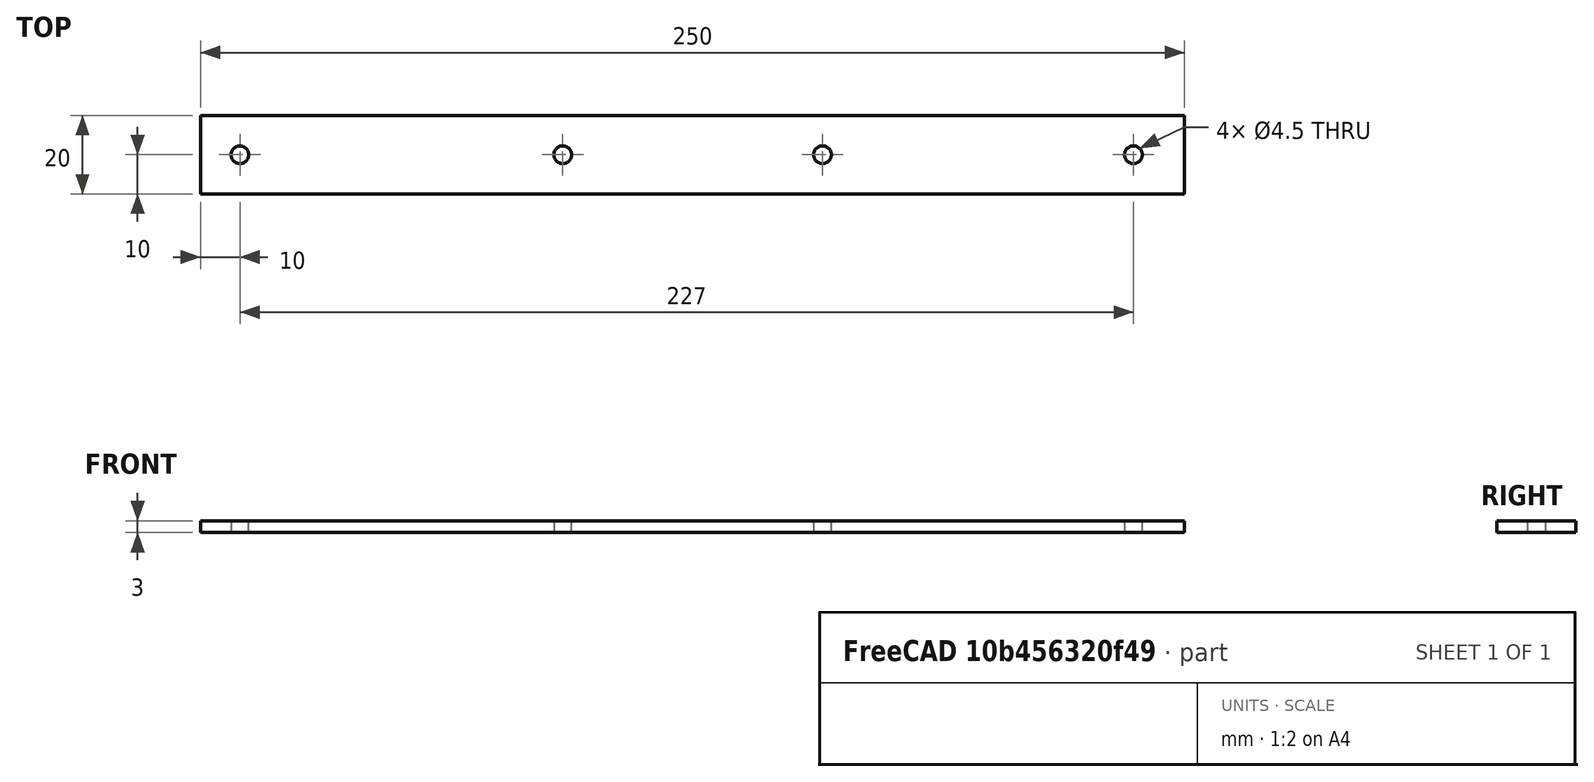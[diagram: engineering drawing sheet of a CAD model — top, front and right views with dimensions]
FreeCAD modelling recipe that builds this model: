
FCSTD DOCUMENT  (FreeCAD 0.21R33668 +26 (Git))
Label: 1-folding-hinge-rear-bar
License: All rights reserved
LicenseURL: http://en.wikipedia.org/wiki/All_rights_reserved
objects: PartDesign::SubtractiveCylinder×4, PartDesign::AdditiveBox×1, PartDesign::Body×1
note: 11 computed .brp shape members not serialized (recipe doc carries the construction recipe); baked Part::Feature solids carry a one-line shape summary decoded from their .brp

FEATURE [PartDesign::AdditiveBox] Box  label="bar"
  AttacherType = Attacher::AttachEngine3D
  Height = 3
  Length = 250
  Width = 20
FEATURE [PartDesign::SubtractiveCylinder] Cylinder  label="mp1"
  Angle = 360
  AttacherType = Attacher::AttachEngine3D
  AttachmentOffset = pos=(10,10,-3) rot=(0,0,1;0rad)
  BaseFeature = -> Box
  FirstAngle = 0
  Height = 3
  MapMode = 5
  Placement = pos=(10,10,0) rot=(0,0,1;0rad)
  Radius = 2.25
  SecondAngle = 0
  Support = -> [Box]
FEATURE [PartDesign::SubtractiveCylinder] Cylinder001  label="mp2"
  Angle = 360
  AttacherType = Attacher::AttachEngine3D
  AttachmentOffset = pos=(227,0,-3) rot=(0,0,1;0rad)
  BaseFeature = -> Cylinder
  FirstAngle = 0
  Height = 3
  MapMode = 5
  Placement = pos=(237,10,0) rot=(0,0,1;0rad)
  Radius = 2.25
  SecondAngle = 0
  Support = -> [Cylinder]
FEATURE [PartDesign::SubtractiveCylinder] Cylinder002  label="hinge-mp1"
  Angle = 360
  AttacherType = Attacher::AttachEngine3D
  AttachmentOffset = pos=(-145,0,-3) rot=(0,0,1;0rad)
  BaseFeature = -> Cylinder001
  FirstAngle = 0
  Height = 3
  MapMode = 5
  Placement = pos=(92,10,0) rot=(0,0,1;0rad)
  Radius = 2.25
  SecondAngle = 0
  Support = -> [Cylinder001]
FEATURE [PartDesign::SubtractiveCylinder] Cylinder003  label="hinge-mp2"
  Angle = 360
  AttacherType = Attacher::AttachEngine3D
  AttachmentOffset = pos=(66,0,-3) rot=(0,0,1;0rad)
  BaseFeature = -> Cylinder002
  FirstAngle = 0
  Height = 3
  MapMode = 5
  Placement = pos=(158,10,0) rot=(0,0,1;0rad)
  Radius = 2.25
  SecondAngle = 0
  Support = -> [Cylinder002]
FEATURE [PartDesign::Body] Body
  Group = -> [Box,Cylinder,Cylinder001,Cylinder002,Cylinder003]
  Origin = -> Origin
  Tip = -> Cylinder003
